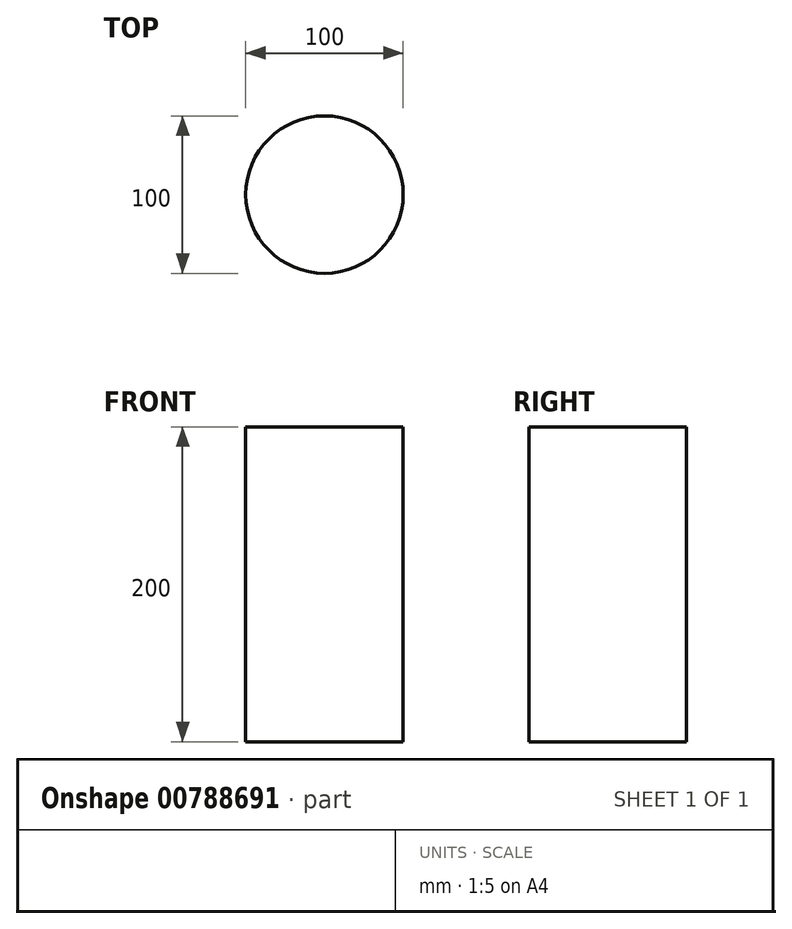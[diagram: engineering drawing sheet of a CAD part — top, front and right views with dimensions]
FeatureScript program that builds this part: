
annotation { "Feature Type Name" : "Feature", "Feature Type Description" : "" }
export const myFeature = defineFeature(function(context is Context, id is Id, definition is map)
    precondition{}
    {
        {
            var Q0;
            Q0=qCreatedBy(makeId("Top.planeOp"),FACE);
            var sketch = newSketch(context, id + "F0", { "sketchPlane" : qUnion([Q0])});
            skCircle(sketch, "E0", {"center": v(0, 0) * mm, "radius": 50 * mm});
            skSolve(sketch);
        }
        {
            var Q0;
            Q0=makeQuery(id+"F0.imprint","IMPRINT",FACE,{"disambiguationData":[TD([[makeQuery(id+"F0.imprint","IMPRINT",EDGE,{"derivedFrom":sQuery(id+"F0.wireOp",EDGE,"E0")}),1.0]])]});
            extrude(context, id + "F1", {"entities" : qUnion([Q0]), "depth" : 200 * mm, "offsetDistance" : 25 * mm});
        }
    });
